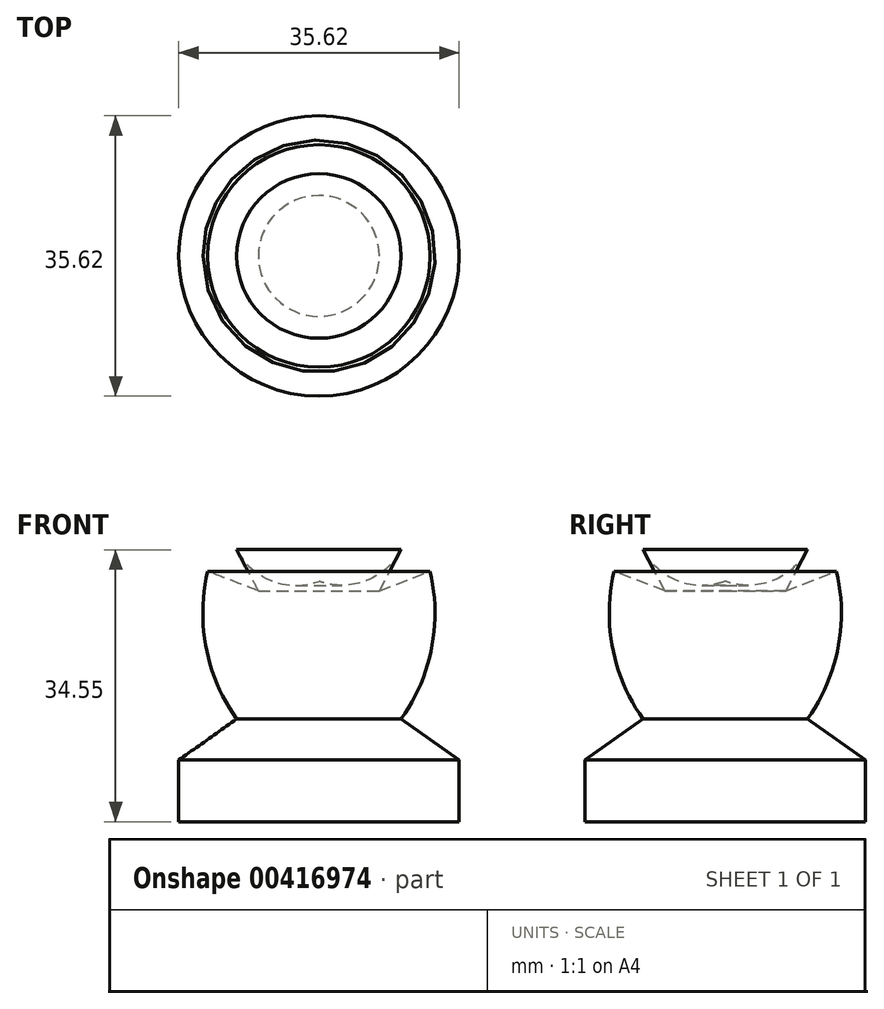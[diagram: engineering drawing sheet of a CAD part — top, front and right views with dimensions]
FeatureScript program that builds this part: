
annotation { "Feature Type Name" : "Feature", "Feature Type Description" : "" }
export const myFeature = defineFeature(function(context is Context, id is Id, definition is map)
    precondition{}
    {
        {
            var Q0;
            Q0=qCreatedBy(makeId("Front.planeOp"),FACE);
            var sketch = newSketch(context, id + "F0", { "sketchPlane" : qUnion([Q0])});
            skLineSegment(sketch, "E0", {"start": v(17.81, 0) * mm, "end": v(17.81, 7.83) * mm});
            skLineSegment(sketch, "E1", {"start": v(17.81, 7.83) * mm, "end": v(10.44, 13.05) * mm});
            skArc(sketch, "E2", {"start": v(10.44, 13.05) * mm, "mid": v(14.3, 22.02) * mm, "end": v(14.13, 31.79) * mm});
            skPoint(sketch, "E2.endSnap0", {"position": v(14.13, 10.44) * mm});
            skLineSegment(sketch, "E3", {"start": v(14.13, 31.79) * mm, "end": v(7.68, 29.33) * mm});
            skLineSegment(sketch, "E4", {"start": v(7.68, 29.33) * mm, "end": v(10.44, 34.55) * mm});
            skArc(sketch, "E5", {"start": v(10.44, 34.55) * mm, "mid": v(9.34, 44.13) * mm, "end": v(0, 46.53) * mm});
            skLineSegment(sketch, "E6", {"start": v(17.81, 0) * mm, "end": v(0, 0) * mm});
            skLineSegment(sketch, "E7", {"start": v(0, 0) * mm, "end": v(0, 46.53) * mm});
            skSolve(sketch);
        }
        {
            var Q0;
            Q0=makeQuery(id+"F0.imprint","IMPRINT",FACE,{"disambiguationData":[TD([[makeQuery(id+"F0.imprint","IMPRINT",EDGE,{"derivedFrom":sQuery(id+"F0.wireOp",EDGE,"E0")}),1.0]])]});
            var Q1;
            Q1=sQuery(id+"F0.wireOp",EDGE,"E7");
            revolve(context, id + "F1", {"entities" : qUnion([Q0]), "axis" : qUnion([Q1]), "revolveType" : RevolveType.FULL});
        }
    });
